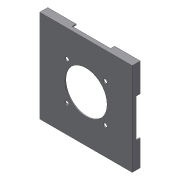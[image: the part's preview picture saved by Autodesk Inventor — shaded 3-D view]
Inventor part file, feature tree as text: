
AUTODESK INVENTOR PART (.ipt)
format: ipt  version: 2017 (Build 210142000, 142)  size: 226,816 bytes
history: native  units: mm
features: sketch x7, extrude x5, projected_geometry x3, hole x1, pattern_circular x1
ambient origin geometry x8: Origin, YZ Plane, XZ Plane, XY Plane, X Axis, Y Axis, Z Axis, Center Point
bodies: Solid1 (feature_tree)
feature tree (17):
  extrude  "Extrusion1"  Depth=90.0mm
  sketch  "Sketch2"  dims[d2=92.0mm d3=92.0mm]
  extrude  "Extrusion2"  Depth=92.0mm
  extrude  "Extrusion3"  Depth=90.0mm
  hole  "Hole1"  [1 undecoded]
  pattern_circular  "Circular Pattern2"  [2 undecoded]
  extrude  "Extrusion4"  Depth=17.25mm
  extrude  "Extrusion5"  Depth=7.0mm TaperAngle=0.0deg
  sketch  "Sketch1"  dims[d0=90.0mm d1=90.0mm]
  projected_geometry  "Projected Loop1"
  sketch  "Sketch3"  dims[d4=1.0mm d5=0.0mm d6=90.0mm]
  sketch  "Sketch4"  dims[d7=90.0mm d8=1.0mm]
  projected_geometry  "Projected Loop2"
  projected_geometry  "Projected Loop3"
  sketch  "Sketch5"  dims[d9=1.0mm]
  sketch  "Sketch6"  dims[d10=10.0mm]
  sketch  "Sketch7"  dims[d11=10.0mm d12=14.5mm d13=17.25mm d14=7.0mm d15=0.0mm d16=22.5mm d17=8.625mm d18=10.0mm d19=0.0mm d23=27.0mm d24=27.0mm d25=4.0mm d26=6.0mm d27=4.0mm d28=2.0mm d29=90.0deg d30=8.0mm d31=20.594885mm d32=40.0mm d33=360.0deg d35=42.0mm d36=10.0mm d37=0.0mm d38=90.0mm d39=90.0mm d40=3.0mm d41=0.0mm]
note: 3 required parameter values undecoded (feature->parameter linkage not recoverable at this tier; creation-order binding heuristic only, values carry confidence <= 0.55)
